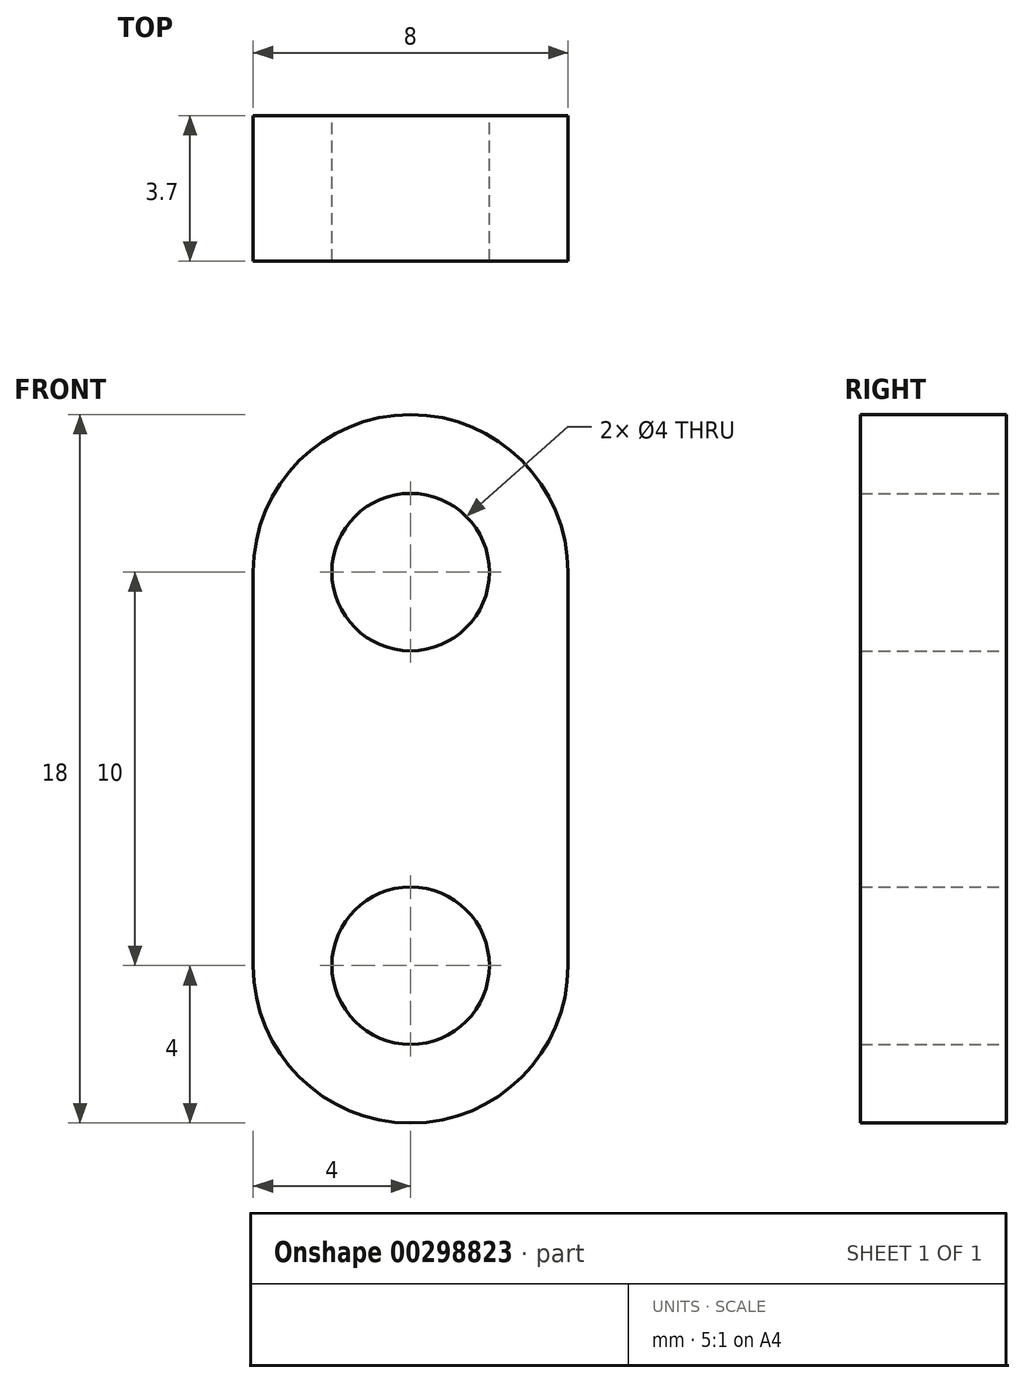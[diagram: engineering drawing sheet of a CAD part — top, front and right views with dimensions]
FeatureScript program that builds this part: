
annotation { "Feature Type Name" : "Feature", "Feature Type Description" : "" }
export const myFeature = defineFeature(function(context is Context, id is Id, definition is map)
    precondition{}
    {
        {
            var Q0;
            Q0=qCreatedBy(makeId("Front.planeOp"),FACE);
            var sketch = newSketch(context, id + "F0", { "sketchPlane" : qUnion([Q0])});
            skCircle(sketch, "E0", {"center": v(0, 0) * mm, "radius": 2 * mm});
            skArc(sketch, "E1", {"start": v(4, 0) * mm, "mid": v(0, 4) * mm, "end": v(-4, 0) * mm});
            skLineSegment(sketch, "E2", {"start": v(-4, 0) * mm, "end": v(-4, -10) * mm});
            skLineSegment(sketch, "E3", {"start": v(4, -10) * mm, "end": v(4, 0) * mm});
            skArc(sketch, "E4", {"start": v(-4, -10) * mm, "mid": v(0, -14) * mm, "end": v(4, -10) * mm});
            skCircle(sketch, "E5", {"center": v(0, -10) * mm, "radius": 2 * mm});
            skSolve(sketch);
        }
        {
            var Q0;
            Q0=makeQuery(id+"F0.imprint","IMPRINT",FACE,{"disambiguationData":[TD([[makeQuery(id+"F0.imprint","IMPRINT",EDGE,{"derivedFrom":sQuery(id+"F0.wireOp",EDGE,"E0")}),-1.0]])]});
            extrude(context, id + "F1", {"entities" : qUnion([Q0]), "depth" : 3.7 * mm});
        }
    });
